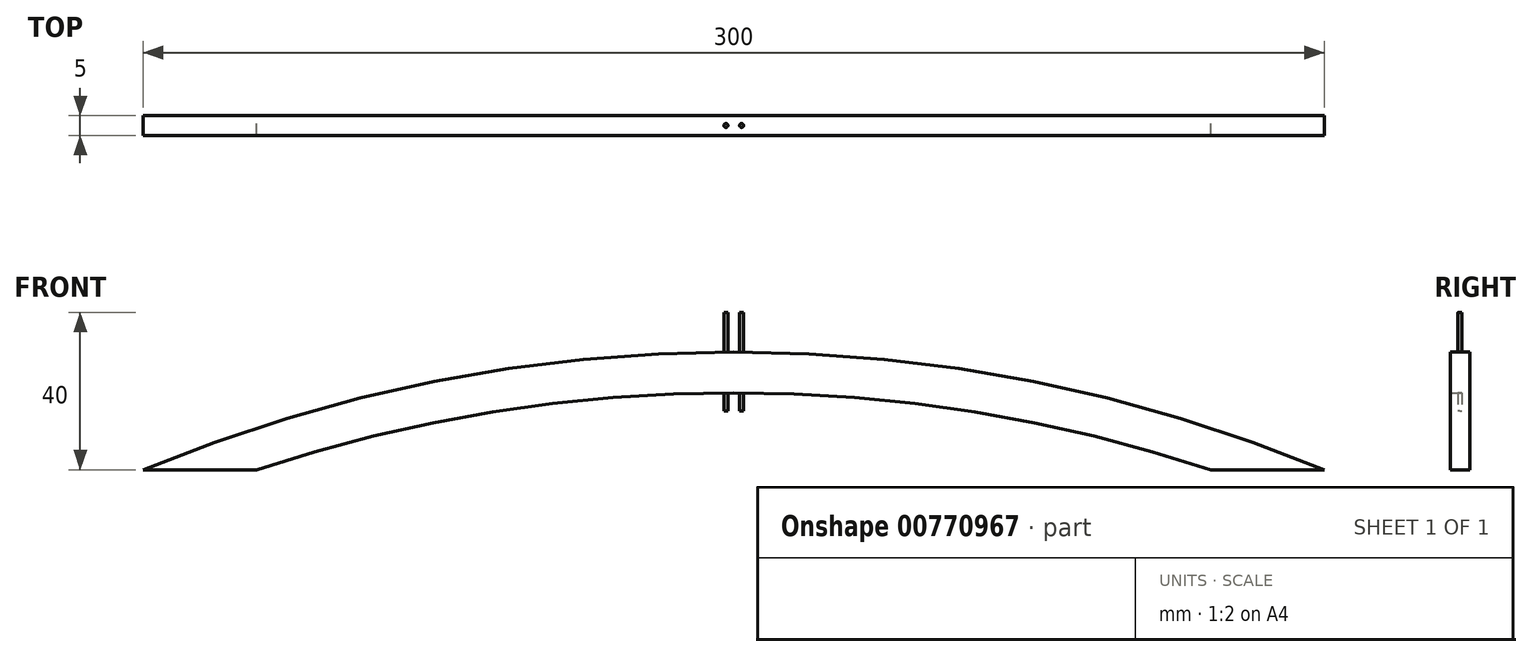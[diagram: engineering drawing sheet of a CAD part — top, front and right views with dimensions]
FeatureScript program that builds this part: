
annotation { "Feature Type Name" : "Feature", "Feature Type Description" : "" }
export const myFeature = defineFeature(function(context is Context, id is Id, definition is map)
    precondition{}
    {
        {
            var Q0;
            Q0=qCreatedBy(makeId("Front.planeOp"),FACE);
            var sketch = newSketch(context, id + "F0", { "sketchPlane" : qUnion([Q0])});
            skLineSegment(sketch, "E0.bottom", {"start": v(150, 15) * mm, "end": v(-150, 15) * mm});
            skLineSegment(sketch, "E0.top", {"start": v(150, -15) * mm, "end": v(-150, -15) * mm});
            skLineSegment(sketch, "E0.left", {"start": v(150, 15) * mm, "end": v(150, -15) * mm});
            skLineSegment(sketch, "E0.right", {"start": v(-150, 15) * mm, "end": v(-150, -15) * mm});
            skPoint(sketch, "E0.middle", {"position": v(0, 0) * mm});
            skArc(sketch, "E1", {"start": v(150, -15) * mm, "mid": v(0, 14.92) * mm, "end": v(-150, -15) * mm});
            skArc(sketch, "E2", {"start": v(121.26, -15) * mm, "mid": v(0, 4.57) * mm, "end": v(-121.26, -15) * mm});
            skLineSegment(sketch, "E3", {"start": v(-121.26, -15) * mm, "end": v(-150, -15) * mm});
            skLineSegment(sketch, "E4", {"start": v(121.26, -15) * mm, "end": v(150, -15) * mm});
            skSolve(sketch);
        }
        {
            var Q0;
            Q0=makeQuery(id+"F0.imprint","IMPRINT",FACE,{"disambiguationData":[TD([[makeQuery(id+"F0.imprint","IMPRINT",EDGE,{"derivedFrom":sQuery(id+"F0.wireOp",EDGE,"E1")}),1.0]])]});
            extrude(context, id + "F1", {"entities" : qUnion([Q0]), "endBound" : BoundingType.SYMMETRIC, "depth" : 5 * mm, "offsetDistance" : 25 * mm});
        }
        {
            var Q0;
            Q0=qCreatedBy(makeId("Top.planeOp"),FACE);
            var sketch = newSketch(context, id + "F2", { "sketchPlane" : qUnion([Q0])});
            skLineSegment(sketch, "E5", {"start": v(0, 0) * mm, "end": v(2, 0) * mm});
            skLineSegment(sketch, "E6", {"start": v(2, 0) * mm, "end": v(0, 0) * mm});
            skLineSegment(sketch, "E7", {"start": v(0, 0) * mm, "end": v(-2, 0) * mm});
            skCircle(sketch, "E8", {"center": v(-2, 0) * mm, "radius": 0.5 * mm});
            skCircle(sketch, "E9", {"center": v(2, 0) * mm, "radius": 0.5 * mm});
            skSolve(sketch);
        }
        {
            var Q0;
            Q0=makeQuery(id+"F2.imprint","IMPRINT",FACE,{"disambiguationData":[TD([[makeQuery(id+"F2.imprint","IMPRINT",EDGE,{"derivedFrom":sQuery(id+"F2.wireOp",EDGE,"E8")}),1.0]])]});
            var Q1;
            Q1=makeQuery(id+"F2.imprint","IMPRINT",FACE,{"disambiguationData":[TD([[makeQuery(id+"F2.imprint","IMPRINT",EDGE,{"derivedFrom":sQuery(id+"F2.wireOp",EDGE,"E9")}),1.0]])]});
            extrude(context, id + "F3", {"entities" : qUnion([Q0, Q1]), "operationType" : NewBodyOperationType.ADD, "depth" : 25 * mm, "offsetDistance" : 25 * mm});
        }
    });
